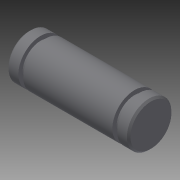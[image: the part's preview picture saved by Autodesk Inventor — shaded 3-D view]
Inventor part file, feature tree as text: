
AUTODESK INVENTOR PART (.ipt)
format: ipt  version: 2014 (Build 180170000, 170)  size: 134,144 bytes
history: native  units: in
note: dims shown in document units (in); Inventor stores cm internally (conversion verified against a paired STEP export)
features: other x49, revolve x1, sketch x1
ambient origin geometry x8: Origin, YZ Plane, XZ Plane, XY Plane, X Axis, Y Axis, Z Axis, Center Point
bodies: Solid1 (feature_tree)
feature tree (51):
  revolve  "Revolution1"  [1 undecoded]
  other  "p1_XY"
  other  "p1_YZ"
  other  "p1_ZX"
  other  "p1_X"
  other  "p1_Y"
  other  "p1_Z"
  other  "p1_Center"
  other  "p2_XY"
  other  "p2_YZ"
  other  "p2_ZX"
  other  "p2_X"
  other  "p2_Y"
  other  "p2_Z"
  other  "p2_Center"
  other  "pin_XY"
  other  "pin_YZ"
  other  "pin_ZX"
  other  "pin_X"
  other  "pin_Y"
  other  "pin_Z"
  other  "pin_Center"
  other  "rr1_XY"
  other  "rr1_YZ"
  other  "rr1_ZX"
  other  "rr1_X"
  other  "rr1_Y"
  other  "rr1_Z"
  other  "rr1_Center"
  other  "rr2_XY"
  other  "rr2_YZ"
  other  "rr2_ZX"
  other  "rr2_X"
  other  "rr2_Y"
  other  "rr2_Z"
  other  "rr2_Center"
  other  "w21_XY"
  other  "w21_YZ"
  other  "w21_ZX"
  other  "w21_X"
  other  "w21_Y"
  other  "w21_Z"
  other  "w21_Center"
  other  "w22_XY"
  other  "w22_YZ"
  other  "w22_ZX"
  other  "w22_X"
  other  "w22_Y"
  other  "w22_Z"
  other  "w22_Center"
  sketch  "Sketch_1"  dims[d0=360.0deg]
note: 1 required parameter value undecoded (feature->parameter linkage not recoverable at this tier; creation-order binding heuristic only, values carry confidence <= 0.55)
